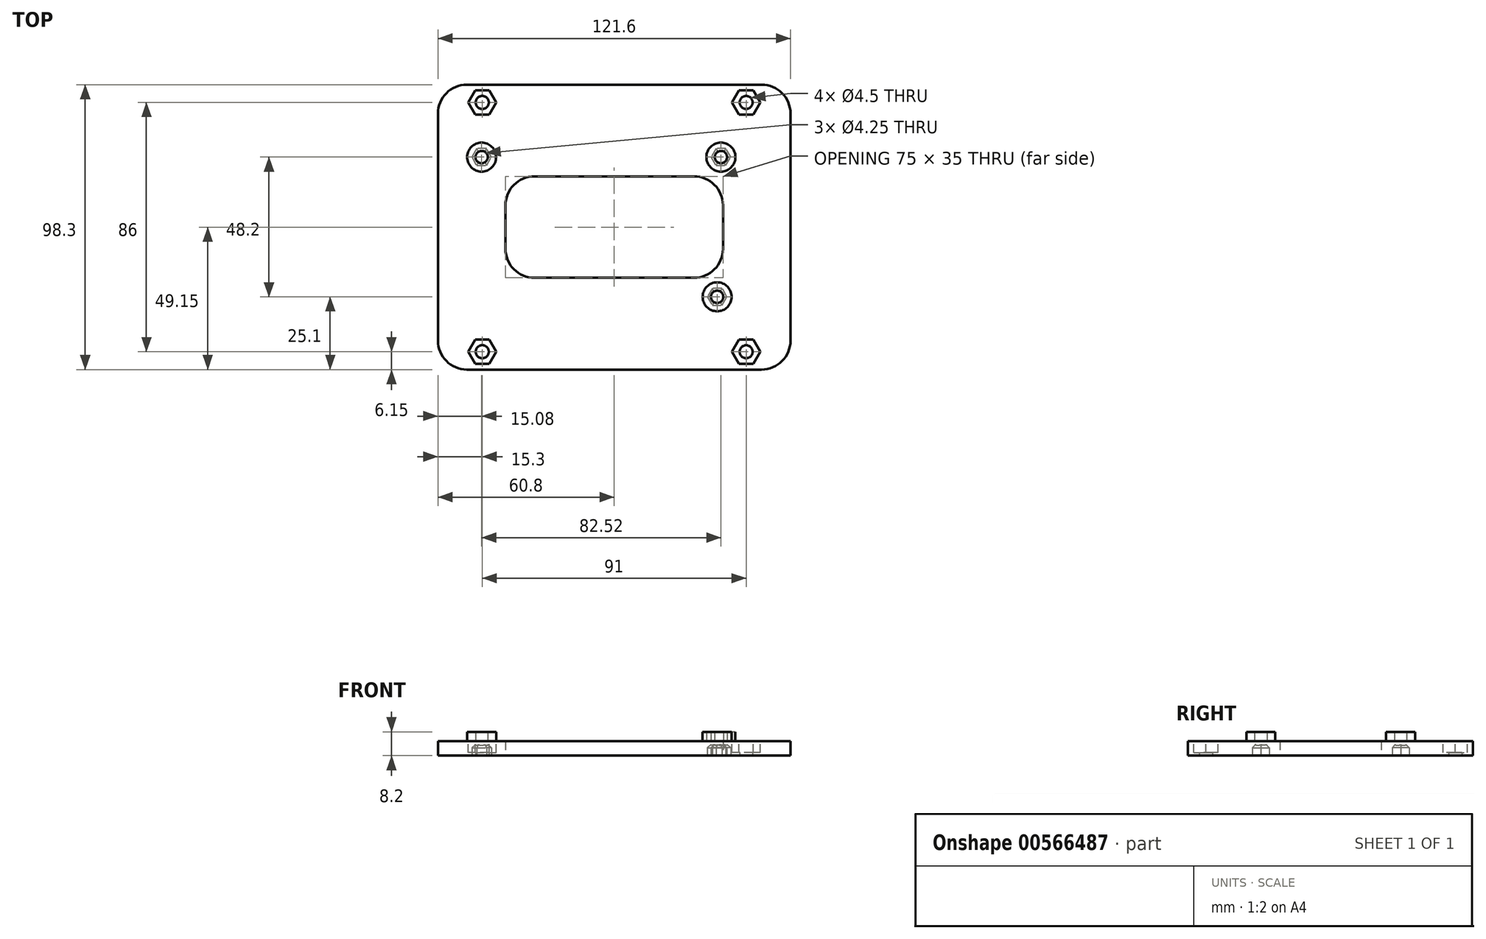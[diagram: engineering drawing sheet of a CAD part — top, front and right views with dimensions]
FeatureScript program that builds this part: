
annotation { "Feature Type Name" : "Feature", "Feature Type Description" : "" }
export const myFeature = defineFeature(function(context is Context, id is Id, definition is map)
    precondition{}
    {
        {
            var Q0;
            Q0=qCreatedBy(makeId("Top.planeOp"),FACE);
            var sketch = newSketch(context, id + "F0", { "sketchPlane" : qUnion([Q0])});
            skLineSegment(sketch, "E0.rect.bottom", {"start": v(50.8, -26.65) * mm, "end": v(-50.8, -26.65) * mm, "construction": true});
            skLineSegment(sketch, "E0.rect.top", {"start": v(50.8, 26.65) * mm, "end": v(-50.8, 26.65) * mm, "construction": true});
            skLineSegment(sketch, "E0.rect.left", {"start": v(50.8, -26.65) * mm, "end": v(50.8, 26.65) * mm, "construction": true});
            skLineSegment(sketch, "E0.rect.right", {"start": v(-50.8, -26.65) * mm, "end": v(-50.8, 26.65) * mm, "construction": true});
            skPoint(sketch, "E0.rect.middle", {"position": v(0, 0) * mm});
            skCircle(sketch, "E1", {"center": v(36.8, 24.15) * mm, "radius": 2.12 * mm});
            skCircle(sketch, "E2", {"center": v(-45.72, 24.15) * mm, "radius": 2.12 * mm});
            skLineSegment(sketch, "E3.rect.bottom", {"start": v(60.8, -39.15) * mm, "end": v(-60.8, -39.15) * mm});
            skLineSegment(sketch, "E3.rect.top", {"start": v(60.8, 39.15) * mm, "end": v(-60.8, 39.15) * mm});
            skLineSegment(sketch, "E3.rect.left", {"start": v(60.8, -39.15) * mm, "end": v(60.8, 39.15) * mm});
            skLineSegment(sketch, "E3.rect.right", {"start": v(-60.8, -39.15) * mm, "end": v(-60.8, 39.15) * mm});
            skLineSegment(sketch, "E4.rect.bottom", {"start": v(27.5, -17.5) * mm, "end": v(-27.5, -17.5) * mm});
            skLineSegment(sketch, "E4.rect.top", {"start": v(27.5, 17.5) * mm, "end": v(-27.5, 17.5) * mm});
            skLineSegment(sketch, "E4.rect.left", {"start": v(37.5, -7.5) * mm, "end": v(37.5, 7.5) * mm});
            skLineSegment(sketch, "E4.rect.right", {"start": v(-37.5, -7.5) * mm, "end": v(-37.5, 7.5) * mm});
            skPoint(sketch, "E5.visualSharp", {"position": v(-37.5, 17.5) * mm});
            skArc(sketch, "E5.filletArc", {"start": v(-27.5, 17.5) * mm, "mid": v(-34.57, 14.57) * mm, "end": v(-37.5, 7.5) * mm});
            skPoint(sketch, "E6.visualSharp", {"position": v(-37.5, -17.5) * mm});
            skArc(sketch, "E6.filletArc", {"start": v(-37.5, -7.5) * mm, "mid": v(-34.57, -14.57) * mm, "end": v(-27.5, -17.5) * mm});
            skPoint(sketch, "E7.visualSharp", {"position": v(37.5, -17.5) * mm});
            skArc(sketch, "E7.filletArc", {"start": v(27.5, -17.5) * mm, "mid": v(34.57, -14.57) * mm, "end": v(37.5, -7.5) * mm});
            skPoint(sketch, "E8.visualSharp", {"position": v(37.5, 17.5) * mm});
            skArc(sketch, "E8.filletArc", {"start": v(37.5, 7.5) * mm, "mid": v(34.57, 14.57) * mm, "end": v(27.5, 17.5) * mm});
            skCircle(sketch, "E9", {"center": v(35.5, -24.05) * mm, "radius": 2.12 * mm});
            skSolve(sketch);
        }
        {
            var Q0;
            Q0=qSketchRegion(id+"F0",true);
            extrude(context, id + "F1", {"entities" : qUnion([Q0]), "depth" : 5 * mm, "offsetDistance" : 25 * mm});
        }
        {
            var Q0;
            Q0=makeQuery(id+"F1.opExtrude","CAP_FACE",FACE,{"disambiguationData":[OSD([sQuery(id+"F0.wireOp",EDGE,"E1"),sQuery(id+"F0.wireOp",EDGE,"E2"),sQuery(id+"F0.wireOp",EDGE,"427397f8-0dd3-485f-8eed-9c75a59d67ec"),sQuery(id+"F0.wireOp",EDGE,"E3.rect.bottom"),sQuery(id+"F0.wireOp",EDGE,"E3.rect.top"),sQuery(id+"F0.wireOp",EDGE,"E3.rect.left"),sQuery(id+"F0.wireOp",EDGE,"E3.rect.right"),sQuery(id+"F0.wireOp",EDGE,"E4.rect.bottom"),sQuery(id+"F0.wireOp",EDGE,"E4.rect.top"),sQuery(id+"F0.wireOp",EDGE,"E4.rect.left"),sQuery(id+"F0.wireOp",EDGE,"E4.rect.right")])],"isStart":false});
            var sketch = newSketch(context, id + "F2", { "sketchPlane" : qUnion([Q0])});
            skCircle(sketch, "E10", {"center": v(-45.72, 24.15) * mm, "radius": 5 * mm});
            skCircle(sketch, "E11", {"center": v(36.8, 24.15) * mm, "radius": 5 * mm});
            skCircle(sketch, "E12", {"center": v(-45.72, 24.15) * mm, "radius": 2.12 * mm});
            skCircle(sketch, "E13", {"center": v(36.8, 24.15) * mm, "radius": 2.12 * mm});
            skLineSegment(sketch, "E14", {"start": v(0, 0) * mm, "end": v(17.05, 0) * mm, "construction": true});
            skCircle(sketch, "E15", {"center": v(35.5, -24.05) * mm, "radius": 5 * mm});
            skCircle(sketch, "E16", {"center": v(35.5, -24.05) * mm, "radius": 2.12 * mm});
            skSolve(sketch);
        }
        {
            var Q0;
            Q0=qSketchRegion(id+"F2",true);
            extrude(context, id + "F3", {"entities" : qUnion([Q0]), "operationType" : NewBodyOperationType.ADD, "depth" : 3.2 * mm});
        }
        {
            var Q0;
            Q0=makeQuery(id+"F1.opExtrude","CAP_FACE",FACE,{"disambiguationData":[OSD([sQuery(id+"F0.wireOp",EDGE,"E1"),sQuery(id+"F0.wireOp",EDGE,"E2"),sQuery(id+"F0.wireOp",EDGE,"427397f8-0dd3-485f-8eed-9c75a59d67ec"),sQuery(id+"F0.wireOp",EDGE,"E3.rect.bottom"),sQuery(id+"F0.wireOp",EDGE,"E3.rect.top"),sQuery(id+"F0.wireOp",EDGE,"E3.rect.left"),sQuery(id+"F0.wireOp",EDGE,"E3.rect.right"),sQuery(id+"F0.wireOp",EDGE,"E4.rect.bottom"),sQuery(id+"F0.wireOp",EDGE,"E4.rect.top"),sQuery(id+"F0.wireOp",EDGE,"E4.rect.left"),sQuery(id+"F0.wireOp",EDGE,"E4.rect.right")])],"isStart":true});
            var sketch = newSketch(context, id + "F4", { "sketchPlane" : qUnion([Q0])});
            skCircle(sketch, "E17.cCircle", {"center": v(-45.72, -24.15) * mm, "radius": 2.93 * mm, "construction": true});
            skLineSegment(sketch, "E17.0", {"start": v(-47.4, -21.23) * mm, "end": v(-44.03, -21.23) * mm});
            skLineSegment(sketch, "E17.1", {"start": v(-44.03, -21.23) * mm, "end": v(-42.34, -24.15) * mm});
            skLineSegment(sketch, "E17.2", {"start": v(-42.34, -24.15) * mm, "end": v(-44.03, -27.08) * mm});
            skLineSegment(sketch, "E17.3", {"start": v(-44.03, -27.08) * mm, "end": v(-47.4, -27.08) * mm});
            skLineSegment(sketch, "E17.4", {"start": v(-47.4, -27.08) * mm, "end": v(-49.1, -24.15) * mm});
            skLineSegment(sketch, "E17.5", {"start": v(-49.1, -24.15) * mm, "end": v(-47.4, -21.23) * mm});
            skPoint(sketch, "E17.0.midPoint", {"position": v(-45.72, -21.23) * mm});
            skCircle(sketch, "E18.cCircle", {"center": v(36.8, -24.15) * mm, "radius": 2.93 * mm, "construction": true});
            skLineSegment(sketch, "E18.0", {"start": v(35.11, -21.22) * mm, "end": v(38.49, -21.22) * mm});
            skLineSegment(sketch, "E18.1", {"start": v(38.49, -21.22) * mm, "end": v(40.18, -24.15) * mm});
            skLineSegment(sketch, "E18.2", {"start": v(40.18, -24.15) * mm, "end": v(38.49, -27.08) * mm});
            skLineSegment(sketch, "E18.3", {"start": v(38.49, -27.07) * mm, "end": v(35.11, -27.07) * mm});
            skLineSegment(sketch, "E18.4", {"start": v(35.11, -27.08) * mm, "end": v(33.42, -24.15) * mm});
            skLineSegment(sketch, "E18.5", {"start": v(33.42, -24.15) * mm, "end": v(35.11, -21.22) * mm});
            skPoint(sketch, "E18.0.midPoint", {"position": v(36.8, -21.23) * mm});
            skCircle(sketch, "E19.cCircle", {"center": v(35.5, 24.05) * mm, "radius": 2.93 * mm, "construction": true});
            skLineSegment(sketch, "E19.0", {"start": v(37.19, 21.12) * mm, "end": v(33.81, 21.12) * mm});
            skLineSegment(sketch, "E19.1", {"start": v(33.81, 21.12) * mm, "end": v(32.12, 24.05) * mm});
            skLineSegment(sketch, "E19.2", {"start": v(32.12, 24.05) * mm, "end": v(33.81, 26.97) * mm});
            skLineSegment(sketch, "E19.3", {"start": v(33.81, 26.97) * mm, "end": v(37.19, 26.97) * mm});
            skLineSegment(sketch, "E19.4", {"start": v(37.19, 26.97) * mm, "end": v(38.88, 24.05) * mm});
            skLineSegment(sketch, "E19.5", {"start": v(38.88, 24.05) * mm, "end": v(37.19, 21.12) * mm});
            skPoint(sketch, "E19.0.midPoint", {"position": v(35.5, 21.12) * mm});
            skSolve(sketch);
        }
        {
            var Q0;
            Q0=qSketchRegion(id+"F4",true);
            extrude(context, id + "F5", {"entities" : qUnion([Q0]), "operationType" : NewBodyOperationType.REMOVE, "oppositeDirection" : true, "depth" : 4 * mm, "offsetDistance" : 25 * mm});
        }
        {
            var Q0;
            Q0=qCreatedBy(makeId("Top.planeOp"),FACE);
            var sketch = newSketch(context, id + "F6", { "sketchPlane" : qUnion([Q0])});
            skLineSegment(sketch, "E20.bottom", {"start": v(-60.8, 39.15) * mm, "end": v(60.8, 39.15) * mm});
            skLineSegment(sketch, "E20.top", {"start": v(-60.8, 49.15) * mm, "end": v(60.8, 49.15) * mm});
            skLineSegment(sketch, "E20.left", {"start": v(-60.8, 39.15) * mm, "end": v(-60.8, 49.15) * mm});
            skLineSegment(sketch, "E20.right", {"start": v(60.8, 39.15) * mm, "end": v(60.8, 49.15) * mm});
            skCircle(sketch, "E21", {"center": v(-45.5, 43) * mm, "radius": 2.25 * mm});
            skCircle(sketch, "E22.MirrorC", {"center": v(45.5, 43) * mm, "radius": 2.25 * mm});
            skCircle(sketch, "E23.MirrorC", {"center": v(-45.5, -43) * mm, "radius": 2.25 * mm});
            skCircle(sketch, "E24.MirrorC", {"center": v(45.5, -43) * mm, "radius": 2.25 * mm});
            skLineSegment(sketch, "E25.MirrorCS", {"start": v(-60.8, -39.15) * mm, "end": v(-60.8, -49.15) * mm});
            skLineSegment(sketch, "E26.MirrorCS", {"start": v(-60.8, -39.15) * mm, "end": v(60.8, -39.15) * mm});
            skLineSegment(sketch, "E27.MirrorCS", {"start": v(60.8, -39.15) * mm, "end": v(60.8, -49.15) * mm});
            skLineSegment(sketch, "E28.MirrorCS", {"start": v(-60.8, -49.15) * mm, "end": v(60.8, -49.15) * mm});
            skSolve(sketch);
        }
        {
            var Q0;
            Q0=qSketchRegion(id+"F6",true);
            extrude(context, id + "F7", {"entities" : qUnion([Q0]), "operationType" : NewBodyOperationType.ADD, "depth" : 5 * mm, "offsetDistance" : 25 * mm});
        }
        {
            var Q0;
            Q0=makeQuery(id+"F7.opExtrude","SWEPT_EDGE",EDGE,{"disambiguationData":[OSD([sQuery(id+"F6.wireOp",EDGE,"E20.top"),sQuery(id+"F6.wireOp",EDGE,"E20.left")])]});
            var Q1;
            Q1=makeQuery(id+"F7.opExtrude","SWEPT_EDGE",EDGE,{"disambiguationData":[OSD([sQuery(id+"F6.wireOp",EDGE,"E20.top"),sQuery(id+"F6.wireOp",EDGE,"E20.right")])]});
            var Q2;
            Q2=makeQuery(id+"F7.opExtrude","SWEPT_EDGE",EDGE,{"disambiguationData":[OSD([sQuery(id+"F6.wireOp",EDGE,"E25.MirrorCS"),sQuery(id+"F6.wireOp",EDGE,"E28.MirrorCS")])]});
            var Q3;
            Q3=makeQuery(id+"F7.opExtrude","SWEPT_EDGE",EDGE,{"disambiguationData":[OSD([sQuery(id+"F6.wireOp",EDGE,"E27.MirrorCS"),sQuery(id+"F6.wireOp",EDGE,"E28.MirrorCS")])]});
            fillet(context, id + "F8", {"entities" : qUnion([Q0, Q1, Q2, Q3]), "radius" : 10 * mm, "tangentPropagation" : true, "allowEdgeOverflow" : false});
        }
        {
            var Q0;
            Q0=makeQuery(id+"F5.boolean.opBoolean","COPY",EDGE,{"derivedFrom":makeQuery(id+"F5.opExtrude","CAP_EDGE",EDGE,{"disambiguationData":[OSD([sQuery(id+"F4.wireOp",EDGE,"E19.4")])],"isStart":false})});
            var Q1;
            Q1=makeQuery(id+"F5.boolean.opBoolean","COPY",EDGE,{"derivedFrom":makeQuery(id+"F5.opExtrude","CAP_EDGE",EDGE,{"disambiguationData":[OSD([sQuery(id+"F4.wireOp",EDGE,"E19.3")])],"isStart":false})});
            var Q2;
            Q2=makeQuery(id+"F5.boolean.opBoolean","COPY",EDGE,{"derivedFrom":makeQuery(id+"F5.opExtrude","CAP_EDGE",EDGE,{"disambiguationData":[OSD([sQuery(id+"F4.wireOp",EDGE,"E19.2")])],"isStart":false})});
            var Q3;
            Q3=makeQuery(id+"F5.boolean.opBoolean","COPY",EDGE,{"derivedFrom":makeQuery(id+"F5.opExtrude","CAP_EDGE",EDGE,{"disambiguationData":[OSD([sQuery(id+"F4.wireOp",EDGE,"E19.1")])],"isStart":false})});
            var Q4;
            Q4=makeQuery(id+"F5.boolean.opBoolean","COPY",EDGE,{"derivedFrom":makeQuery(id+"F5.opExtrude","CAP_EDGE",EDGE,{"disambiguationData":[OSD([sQuery(id+"F4.wireOp",EDGE,"E19.5")])],"isStart":false})});
            var Q5;
            Q5=makeQuery(id+"F5.boolean.opBoolean","COPY",EDGE,{"derivedFrom":makeQuery(id+"F5.opExtrude","CAP_EDGE",EDGE,{"disambiguationData":[OSD([sQuery(id+"F4.wireOp",EDGE,"E19.0")])],"isStart":false})});
            var Q6;
            Q6=makeQuery(id+"F5.boolean.opBoolean","COPY",EDGE,{"derivedFrom":makeQuery(id+"F5.opExtrude","CAP_EDGE",EDGE,{"disambiguationData":[OSD([sQuery(id+"F4.wireOp",EDGE,"E18.0")])],"isStart":false})});
            var Q7;
            Q7=makeQuery(id+"F5.boolean.opBoolean","COPY",EDGE,{"derivedFrom":makeQuery(id+"F5.opExtrude","CAP_EDGE",EDGE,{"disambiguationData":[OSD([sQuery(id+"F4.wireOp",EDGE,"E18.5")])],"isStart":false})});
            var Q8;
            Q8=makeQuery(id+"F5.boolean.opBoolean","COPY",EDGE,{"derivedFrom":makeQuery(id+"F5.opExtrude","CAP_EDGE",EDGE,{"disambiguationData":[OSD([sQuery(id+"F4.wireOp",EDGE,"E18.4")])],"isStart":false})});
            var Q9;
            Q9=makeQuery(id+"F5.boolean.opBoolean","COPY",EDGE,{"derivedFrom":makeQuery(id+"F5.opExtrude","CAP_EDGE",EDGE,{"disambiguationData":[OSD([sQuery(id+"F4.wireOp",EDGE,"E18.1")])],"isStart":false})});
            var Q10;
            Q10=makeQuery(id+"F5.boolean.opBoolean","COPY",EDGE,{"derivedFrom":makeQuery(id+"F5.opExtrude","CAP_EDGE",EDGE,{"disambiguationData":[OSD([sQuery(id+"F4.wireOp",EDGE,"E18.2")])],"isStart":false})});
            var Q11;
            Q11=makeQuery(id+"F5.boolean.opBoolean","COPY",EDGE,{"derivedFrom":makeQuery(id+"F5.opExtrude","CAP_EDGE",EDGE,{"disambiguationData":[OSD([sQuery(id+"F4.wireOp",EDGE,"E18.3")])],"isStart":false})});
            var Q12;
            Q12=makeQuery(id+"F5.boolean.opBoolean","COPY",EDGE,{"derivedFrom":makeQuery(id+"F5.opExtrude","CAP_EDGE",EDGE,{"disambiguationData":[OSD([sQuery(id+"F4.wireOp",EDGE,"E17.2")])],"isStart":false})});
            var Q13;
            Q13=makeQuery(id+"F5.boolean.opBoolean","COPY",EDGE,{"derivedFrom":makeQuery(id+"F5.opExtrude","CAP_EDGE",EDGE,{"disambiguationData":[OSD([sQuery(id+"F4.wireOp",EDGE,"E17.3")])],"isStart":false})});
            var Q14;
            Q14=makeQuery(id+"F5.boolean.opBoolean","COPY",EDGE,{"derivedFrom":makeQuery(id+"F5.opExtrude","CAP_EDGE",EDGE,{"disambiguationData":[OSD([sQuery(id+"F4.wireOp",EDGE,"E17.4")])],"isStart":false})});
            var Q15;
            Q15=makeQuery(id+"F5.boolean.opBoolean","COPY",EDGE,{"derivedFrom":makeQuery(id+"F5.opExtrude","CAP_EDGE",EDGE,{"disambiguationData":[OSD([sQuery(id+"F4.wireOp",EDGE,"E17.1")])],"isStart":false})});
            var Q16;
            Q16=makeQuery(id+"F5.boolean.opBoolean","COPY",EDGE,{"derivedFrom":makeQuery(id+"F5.opExtrude","CAP_EDGE",EDGE,{"disambiguationData":[OSD([sQuery(id+"F4.wireOp",EDGE,"E17.0")])],"isStart":false})});
            var Q17;
            Q17=makeQuery(id+"F5.boolean.opBoolean","COPY",EDGE,{"derivedFrom":makeQuery(id+"F5.opExtrude","CAP_EDGE",EDGE,{"disambiguationData":[OSD([sQuery(id+"F4.wireOp",EDGE,"E17.5")])],"isStart":false})});
            chamfer(context, id + "F9", {"entities" : qUnion([Q0, Q1, Q2, Q3, Q4, Q5, Q6, Q7, Q8, Q9, Q10, Q11, Q12, Q13, Q14, Q15, Q16, Q17]), "width" : 1.25 * mm, "tangentPropagation" : true});
        }
        {
            var Q0;
            Q0=makeQuery(id+"F7.boolean.opBoolean","MERGE",FACE,{"derivedFrom":[makeQuery(id+"F1.opExtrude","CAP_FACE",FACE,{"disambiguationData":[OSD([sQuery(id+"F0.wireOp",EDGE,"E1"),sQuery(id+"F0.wireOp",EDGE,"E2"),sQuery(id+"F0.wireOp",EDGE,"E3.rect.bottom"),sQuery(id+"F0.wireOp",EDGE,"E3.rect.top"),sQuery(id+"F0.wireOp",EDGE,"E3.rect.left"),sQuery(id+"F0.wireOp",EDGE,"E3.rect.right"),sQuery(id+"F0.wireOp",EDGE,"E4.rect.bottom"),sQuery(id+"F0.wireOp",EDGE,"E4.rect.top"),sQuery(id+"F0.wireOp",EDGE,"E4.rect.left"),sQuery(id+"F0.wireOp",EDGE,"E4.rect.right"),sQuery(id+"F0.wireOp",EDGE,"E5.filletArc"),sQuery(id+"F0.wireOp",EDGE,"E6.filletArc"),sQuery(id+"F0.wireOp",EDGE,"E7.filletArc"),sQuery(id+"F0.wireOp",EDGE,"E8.filletArc"),sQuery(id+"F0.wireOp",EDGE,"E9")])],"isStart":false}),makeQuery(id+"F7.opExtrude","CAP_FACE",FACE,{"disambiguationData":[OSD([sQuery(id+"F6.wireOp",EDGE,"E20.bottom"),sQuery(id+"F6.wireOp",EDGE,"E20.top"),sQuery(id+"F6.wireOp",EDGE,"E20.left"),sQuery(id+"F6.wireOp",EDGE,"E20.right"),sQuery(id+"F6.wireOp",EDGE,"E21"),sQuery(id+"F6.wireOp",EDGE,"E22.MirrorC")])],"isStart":false}),makeQuery(id+"F7.opExtrude","CAP_FACE",FACE,{"disambiguationData":[OSD([sQuery(id+"F6.wireOp",EDGE,"E23.MirrorC"),sQuery(id+"F6.wireOp",EDGE,"E24.MirrorC"),sQuery(id+"F6.wireOp",EDGE,"E25.MirrorCS"),sQuery(id+"F6.wireOp",EDGE,"E26.MirrorCS"),sQuery(id+"F6.wireOp",EDGE,"E27.MirrorCS"),sQuery(id+"F6.wireOp",EDGE,"E28.MirrorCS")])],"isStart":false})]});
            var sketch = newSketch(context, id + "F10", { "sketchPlane" : qUnion([Q0])});
            skCircle(sketch, "E29.cCircle", {"center": v(-45.5, 43) * mm, "radius": 4.22 * mm, "construction": true});
            skLineSegment(sketch, "E29.0", {"start": v(-47.94, 47.22) * mm, "end": v(-43.06, 47.22) * mm});
            skLineSegment(sketch, "E29.1", {"start": v(-43.06, 47.22) * mm, "end": v(-40.62, 43) * mm});
            skLineSegment(sketch, "E29.2", {"start": v(-40.62, 43) * mm, "end": v(-43.06, 38.77) * mm});
            skLineSegment(sketch, "E29.3", {"start": v(-43.06, 38.77) * mm, "end": v(-47.94, 38.77) * mm});
            skLineSegment(sketch, "E29.4", {"start": v(-47.94, 38.77) * mm, "end": v(-50.38, 43) * mm});
            skLineSegment(sketch, "E29.5", {"start": v(-50.38, 43) * mm, "end": v(-47.94, 47.23) * mm});
            skPoint(sketch, "E29.0.midPoint", {"position": v(-45.5, 47.22) * mm});
            skLineSegment(sketch, "E30.MirrorCS", {"start": v(50.38, 43) * mm, "end": v(47.94, 47.22) * mm});
            skLineSegment(sketch, "E31.MirrorCS", {"start": v(43.06, 38.77) * mm, "end": v(47.94, 38.77) * mm});
            skLineSegment(sketch, "E32.MirrorCS", {"start": v(47.94, 47.22) * mm, "end": v(43.06, 47.22) * mm});
            skLineSegment(sketch, "E33.MirrorCS", {"start": v(43.06, 47.22) * mm, "end": v(40.62, 43) * mm});
            skPoint(sketch, "E34.MirrorP", {"position": v(45.5, 47.22) * mm});
            skLineSegment(sketch, "E35.MirrorCS", {"start": v(40.62, 43) * mm, "end": v(43.06, 38.78) * mm});
            skCircle(sketch, "E36.MirrorC", {"center": v(45.5, 43) * mm, "radius": 4.22 * mm, "construction": true});
            skLineSegment(sketch, "E37.MirrorCS", {"start": v(47.94, 38.77) * mm, "end": v(50.38, 43) * mm});
            skLineSegment(sketch, "E38.MirrorCS", {"start": v(47.94, -38.77) * mm, "end": v(50.38, -43) * mm});
            skLineSegment(sketch, "E39.MirrorCS", {"start": v(40.62, -43) * mm, "end": v(43.06, -38.78) * mm});
            skLineSegment(sketch, "E40.MirrorCS", {"start": v(43.06, -47.22) * mm, "end": v(40.62, -43) * mm});
            skLineSegment(sketch, "E41.MirrorCS", {"start": v(47.94, -47.22) * mm, "end": v(43.06, -47.22) * mm});
            skCircle(sketch, "E42.MirrorC", {"center": v(45.5, -43) * mm, "radius": 4.22 * mm, "construction": true});
            skLineSegment(sketch, "E43.MirrorCS", {"start": v(50.38, -43) * mm, "end": v(47.94, -47.23) * mm});
            skLineSegment(sketch, "E44.MirrorCS", {"start": v(43.06, -38.77) * mm, "end": v(47.94, -38.77) * mm});
            skPoint(sketch, "E45.MirrorP", {"position": v(45.5, -47.22) * mm});
            skLineSegment(sketch, "E46.MirrorCS", {"start": v(-47.94, -47.22) * mm, "end": v(-43.06, -47.22) * mm});
            skLineSegment(sketch, "E47.MirrorCS", {"start": v(-43.06, -38.77) * mm, "end": v(-47.94, -38.77) * mm});
            skLineSegment(sketch, "E48.MirrorCS", {"start": v(-50.38, -43) * mm, "end": v(-47.94, -47.22) * mm});
            skLineSegment(sketch, "E49.MirrorCS", {"start": v(-43.06, -47.22) * mm, "end": v(-40.62, -43) * mm});
            skLineSegment(sketch, "E50.MirrorCS", {"start": v(-40.62, -43) * mm, "end": v(-43.06, -38.78) * mm});
            skLineSegment(sketch, "E51.MirrorCS", {"start": v(-47.94, -38.77) * mm, "end": v(-50.38, -43) * mm});
            skCircle(sketch, "E52.MirrorC", {"center": v(-45.5, -43) * mm, "radius": 4.22 * mm, "construction": true});
            skPoint(sketch, "E53.MirrorP", {"position": v(-45.5, -47.22) * mm});
            skSolve(sketch);
        }
        {
            var Q0;
            Q0=qSketchRegion(id+"F10",true);
            extrude(context, id + "F11", {"entities" : qUnion([Q0]), "operationType" : NewBodyOperationType.REMOVE, "oppositeDirection" : true, "depth" : 4 * mm, "offsetDistance" : 25 * mm});
        }
    });
